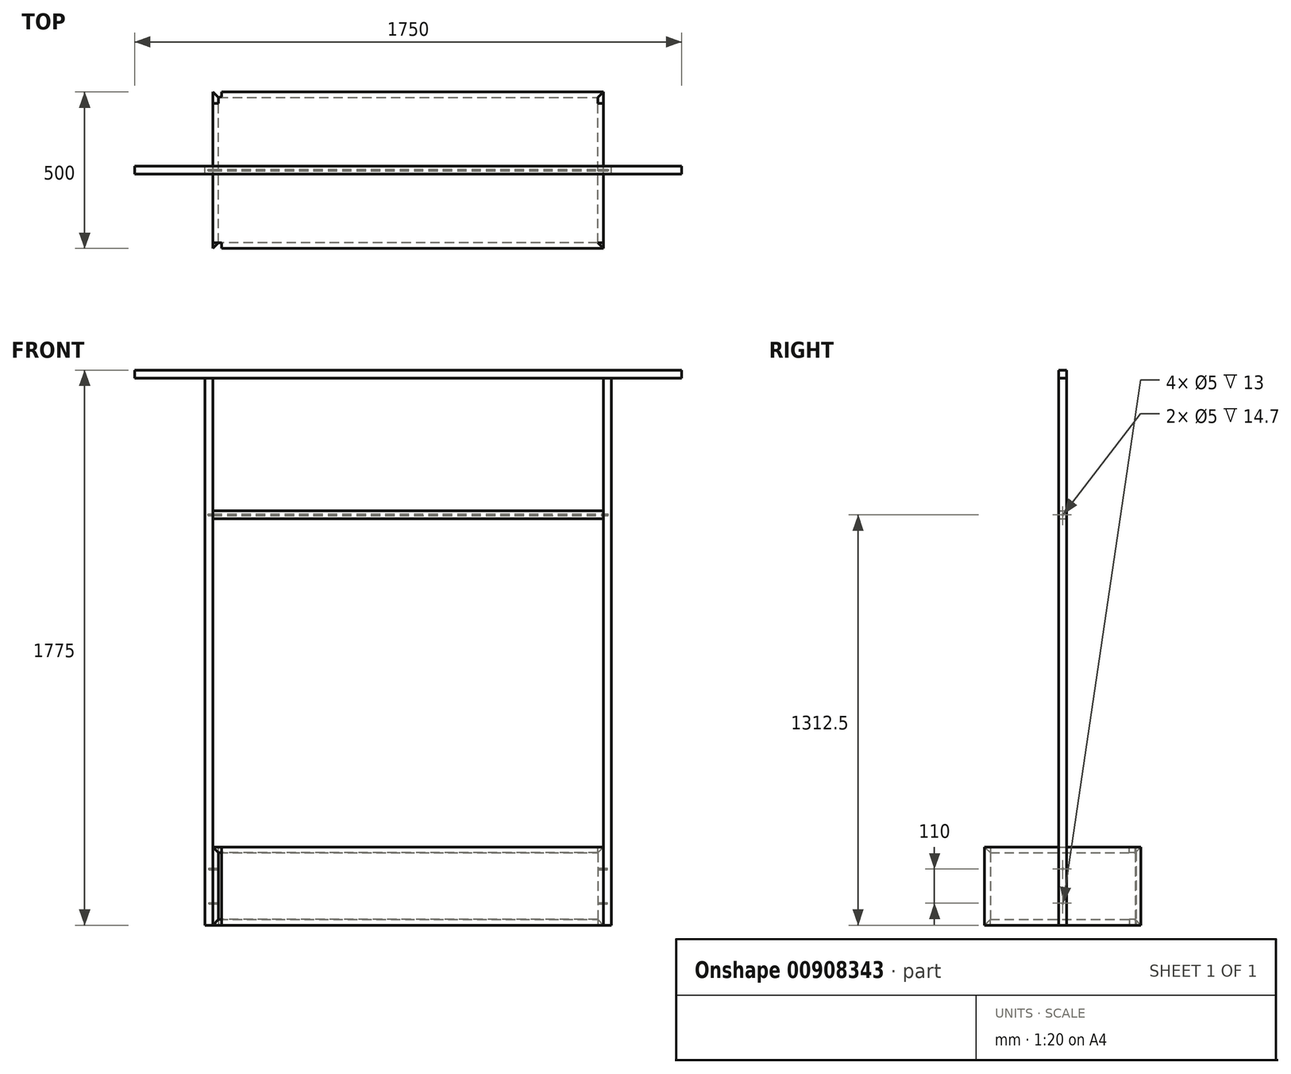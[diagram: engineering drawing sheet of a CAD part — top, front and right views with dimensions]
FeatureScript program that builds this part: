
annotation { "Feature Type Name" : "Feature", "Feature Type Description" : "" }
export const myFeature = defineFeature(function(context is Context, id is Id, definition is map)
    precondition{}
    {
        {
            var Q0;
            Q0=qCreatedBy(makeId("Front.planeOp"),FACE);
            var sketch = newSketch(context, id + "F0", { "sketchPlane" : qUnion([Q0])});
            skLineSegment(sketch, "E0", {"start": v(-625, 0) * mm, "end": v(625, 0) * mm});
            skLineSegment(sketch, "E1", {"start": v(625, 0) * mm, "end": v(607, 18) * mm});
            skLineSegment(sketch, "E2", {"start": v(607, 18) * mm, "end": v(-607, 18) * mm});
            skLineSegment(sketch, "E3", {"start": v(-607, 18) * mm, "end": v(-625, 0) * mm});
            skSolve(sketch);
        }
        {
            var Q0;
            Q0 = qSketchRegion(id + "F0", true);
            extrude(context, id + "F1", {"entities" : qUnion([Q0]), "endBound" : BoundingType.SYMMETRIC, "depth" : 500 * mm, "offsetDistance" : 25 * mm});
        }
        {
            var Q0;
            Q0=qCreatedBy(makeId("Right.planeOp"),FACE);
            var sketch = newSketch(context, id + "F2", { "sketchPlane" : qUnion([Q0])});
            skLineSegment(sketch, "E4", {"start": v(-250, 0) * mm, "end": v(-231.1, 18.9) * mm});
            skLineSegment(sketch, "E5", {"start": v(-231.1, 18.9) * mm, "end": v(-231.1, 28.41) * mm});
            skLineSegment(sketch, "E6", {"start": v(-231.1, 28.41) * mm, "end": v(-266.04, 28.41) * mm});
            skLineSegment(sketch, "E7", {"start": v(-266.04, 28.41) * mm, "end": v(-266.04, 0) * mm});
            skLineSegment(sketch, "E8", {"start": v(-266.04, 0) * mm, "end": v(-250, 0) * mm});
            skLineSegment(sketch, "E9", {"start": v(250, 0) * mm, "end": v(231.1, 18.9) * mm});
            skLineSegment(sketch, "E10", {"start": v(231.1, 18.9) * mm, "end": v(231.1, 44) * mm});
            skLineSegment(sketch, "E11", {"start": v(231.1, 44) * mm, "end": v(262.92, 44) * mm});
            skLineSegment(sketch, "E12", {"start": v(262.92, 44) * mm, "end": v(262.92, 0) * mm});
            skLineSegment(sketch, "E13", {"start": v(250, 0) * mm, "end": v(262.92, 0) * mm});
            skSolve(sketch);
        }
        {
            var Q0;
            Q0 = qSketchRegion(id + "F2", true);
            extrude(context, id + "F3", {"entities" : qUnion([Q0]), "operationType" : NewBodyOperationType.REMOVE, "endBound" : BoundingType.SYMMETRIC, "oppositeDirection" : true, "depth" : 1428 * mm, "offsetDistance" : 25 * mm});
        }
        {
            var Q0;
            Q0=qCreatedBy(makeId("Right.planeOp"),FACE);
            var sketch = newSketch(context, id + "F4", { "sketchPlane" : qUnion([Q0])});
            skLineSegment(sketch, "E14.0", {"start": v(232, 18) * mm, "end": v(250, 0) * mm});
            skLineSegment(sketch, "E14.1", {"start": v(-232, 18) * mm, "end": v(-250, 0) * mm});
            skLineSegment(sketch, "E15", {"start": v(232, 18) * mm, "end": v(232, 232) * mm});
            skLineSegment(sketch, "E16", {"start": v(232, 232) * mm, "end": v(250, 250) * mm});
            skLineSegment(sketch, "E17", {"start": v(250, 250) * mm, "end": v(250, 0) * mm});
            skLineSegment(sketch, "E18", {"start": v(-232, 18) * mm, "end": v(-232, 232) * mm});
            skLineSegment(sketch, "E19", {"start": v(-232, 232) * mm, "end": v(-250, 250) * mm});
            skLineSegment(sketch, "E20", {"start": v(-250, 250) * mm, "end": v(-250, 0) * mm});
            skSolve(sketch);
        }
        {
            var Q0;
            Q0=makeQuery(id+"F4.imprint","IMPRINT",FACE,{"disambiguationData":[TD([[makeQuery(id+"F4.imprint","IMPRINT",EDGE,{"derivedFrom":sQuery(id+"F4.wireOp",EDGE,"E14.0")}),1.0]])]});
            var Q1;
            Q1=makeQuery(id+"F4.imprint","IMPRINT",FACE,{"disambiguationData":[TD([[makeQuery(id+"F4.imprint","IMPRINT",EDGE,{"derivedFrom":sQuery(id+"F4.wireOp",EDGE,"E14.1")}),-1.0]])]});
            var Q2;
            Q2=makeQuery(id+"F1.opExtrude","CAP_VERTEX",VERTEX,{"disambiguationData":[OSD([sQuery(id+"F0.wireOp",EDGE,"E0"),sQuery(id+"F0.wireOp",EDGE,"E1")])],"isStart":true});
            extrude(context, id + "F5", {"entities" : qUnion([Q0, Q1]), "endBound" : BoundingType.SYMMETRIC, "depth" : 1250 * mm, "endBoundEntityVertex" : qUnion([Q2]), "offsetDistance" : 25 * mm});
        }
        {
            var Q0;
            Q0=qCreatedBy(makeId("Top.planeOp"),FACE);
            var sketch = newSketch(context, id + "F6", { "sketchPlane" : qUnion([Q0])});
            skLineSegment(sketch, "E21", {"start": v(-625, 250) * mm, "end": v(-607, 232) * mm});
            skLineSegment(sketch, "E22", {"start": v(-607, 232) * mm, "end": v(-607, 212.8) * mm});
            skLineSegment(sketch, "E23", {"start": v(-607, 212.8) * mm, "end": v(-625, 212.8) * mm});
            skLineSegment(sketch, "E24", {"start": v(-625, 212.8) * mm, "end": v(-625, 250) * mm});
            skLineSegment(sketch, "E25", {"start": v(-607, -232) * mm, "end": v(-625, -250) * mm});
            skLineSegment(sketch, "E26", {"start": v(-625, -250) * mm, "end": v(-638.85, -250) * mm});
            skLineSegment(sketch, "E27", {"start": v(-638.85, -250) * mm, "end": v(-638.85, -232) * mm});
            skLineSegment(sketch, "E28", {"start": v(-638.85, -232) * mm, "end": v(-607, -232) * mm});
            skLineSegment(sketch, "E29.MirrorCS", {"start": v(625, 250) * mm, "end": v(607, 232) * mm});
            skLineSegment(sketch, "E30.MirrorCS", {"start": v(638.85, -232) * mm, "end": v(607, -232) * mm});
            skLineSegment(sketch, "E31.MirrorCS", {"start": v(638.85, -250) * mm, "end": v(638.85, -232) * mm});
            skLineSegment(sketch, "E32.MirrorCS", {"start": v(607, -232) * mm, "end": v(625, -250) * mm});
            skLineSegment(sketch, "E33.MirrorCS", {"start": v(607, 232) * mm, "end": v(607, 212.8) * mm});
            skLineSegment(sketch, "E34.MirrorCS", {"start": v(625, -250) * mm, "end": v(638.85, -250) * mm});
            skLineSegment(sketch, "E35.MirrorCS", {"start": v(607, 212.8) * mm, "end": v(625, 212.8) * mm});
            skLineSegment(sketch, "E36.MirrorCS", {"start": v(625, 212.8) * mm, "end": v(625, 250) * mm});
            skSolve(sketch);
        }
        {
            var Q0;
            Q0 = qSketchRegion(id + "F6", true);
            extrude(context, id + "F7", {"entities" : qUnion([Q0]), "operationType" : NewBodyOperationType.REMOVE, "endBound" : BoundingType.SYMMETRIC, "depth" : 1216 * mm, "offsetDistance" : 25 * mm});
        }
        {
            var Q0;
            Q0=qCreatedBy(makeId("Front.planeOp"),FACE);
            var sketch = newSketch(context, id + "F8", { "sketchPlane" : qUnion([Q0])});
            skLineSegment(sketch, "E37.0", {"start": v(-625, 0) * mm, "end": v(-607, 18) * mm});
            skLineSegment(sketch, "E37.1", {"start": v(-607, 232) * mm, "end": v(-607, 18) * mm});
            skLineSegment(sketch, "E37.2", {"start": v(-625, 250) * mm, "end": v(-625, 0) * mm});
            skLineSegment(sketch, "E37.3", {"start": v(-607, 232) * mm, "end": v(-625, 250) * mm});
            skSolve(sketch);
        }
        {
            var Q0;
            Q0 = qSketchRegion(id + "F8", true);
            extrude(context, id + "F9", {"entities" : qUnion([Q0]), "endBound" : BoundingType.SYMMETRIC, "depth" : 500 * mm, "offsetDistance" : 25 * mm});
        }
        {
            var Q0;
            Q0=qCreatedBy(makeId("Top.planeOp"),FACE);
            var sketch = newSketch(context, id + "F10", { "sketchPlane" : qUnion([Q0])});
            skLineSegment(sketch, "E38.0", {"start": v(-607, -232) * mm, "end": v(-625, -250) * mm});
            skLineSegment(sketch, "E38.1", {"start": v(-607, 232) * mm, "end": v(-625, 250) * mm});
            skLineSegment(sketch, "E39", {"start": v(-625, 250) * mm, "end": v(-625, 288.49) * mm});
            skLineSegment(sketch, "E40", {"start": v(-625, 288.49) * mm, "end": v(-596.8, 288.49) * mm});
            skLineSegment(sketch, "E41", {"start": v(-596.8, 288.49) * mm, "end": v(-596.8, 234.6) * mm});
            skLineSegment(sketch, "E42", {"start": v(-596.8, 234.6) * mm, "end": v(-607, 232) * mm});
            skLineSegment(sketch, "E43", {"start": v(-607, -232) * mm, "end": v(-596.8, -232) * mm});
            skLineSegment(sketch, "E44", {"start": v(-596.8, -232) * mm, "end": v(-596.8, -280.72) * mm});
            skLineSegment(sketch, "E45", {"start": v(-596.8, -280.72) * mm, "end": v(-625, -280.72) * mm});
            skLineSegment(sketch, "E46", {"start": v(-625, -280.72) * mm, "end": v(-625, -250) * mm});
            skSolve(sketch);
        }
        {
            var Q0;
            Q0 = qSketchRegion(id + "F10", true);
            extrude(context, id + "F11", {"entities" : qUnion([Q0]), "operationType" : NewBodyOperationType.REMOVE, "endBound" : BoundingType.SYMMETRIC, "depth" : 1068 * mm, "offsetDistance" : 25 * mm});
        }
        {
            var Q0;
            Q0=makeQuery(id+"F9.opExtrude","SWEPT_BODY",BODY,{"disambiguationData":[OSD([sQuery(id+"F8.wireOp",EDGE,"E37.0"),sQuery(id+"F8.wireOp",EDGE,"E37.1"),sQuery(id+"F8.wireOp",EDGE,"E37.2"),sQuery(id+"F8.wireOp",EDGE,"E37.3")])]});
            var Q1;
            Q1=qCreatedBy(makeId("Right.planeOp"),FACE);
            mirror(context, id + "F12", {"entities" : qUnion([Q0]), "mirrorPlane" : qUnion([Q1])});
        }
        {
            var Q0;
            Q0=qCreatedBy(makeId("Top.planeOp"),FACE);
            cPlane(context, id + "F13", {"entities" : qUnion([Q0]), "cplaneType" : CPlaneType.OFFSET, "offset" : 125 * mm, "width" : 150 * mm, "height" : 150 * mm});
        }
        {
            var Q0;
            Q0=makeQuery(id+"F1.opExtrude","SWEPT_BODY",BODY,{"disambiguationData":[OSD([sQuery(id+"F0.wireOp",EDGE,"E0"),sQuery(id+"F0.wireOp",EDGE,"E1"),sQuery(id+"F0.wireOp",EDGE,"E2"),sQuery(id+"F0.wireOp",EDGE,"E3")])]});
            var Q1;
            Q1=qCreatedBy(id+"F13.planeOp",FACE);
            mirror(context, id + "F14", {"entities" : qUnion([Q0]), "mirrorPlane" : qUnion([Q1])});
        }
        {
            var Q0;
            Q0=qCreatedBy(makeId("Front.planeOp"),FACE);
            var sketch = newSketch(context, id + "F15", { "sketchPlane" : qUnion([Q0])});
            skLineSegment(sketch, "E47.bottom", {"start": v(625, 0) * mm, "end": v(650, 0) * mm});
            skLineSegment(sketch, "E47.top", {"start": v(625, 1750) * mm, "end": v(650, 1750) * mm});
            skLineSegment(sketch, "E47.left", {"start": v(625, 0) * mm, "end": v(625, 1750) * mm});
            skLineSegment(sketch, "E47.right", {"start": v(650, 0) * mm, "end": v(650, 1750) * mm});
            skLineSegment(sketch, "E48.bottom", {"start": v(-625, 0) * mm, "end": v(-650, 0) * mm});
            skLineSegment(sketch, "E48.top", {"start": v(-625, 1750) * mm, "end": v(-650, 1750) * mm});
            skLineSegment(sketch, "E48.left", {"start": v(-625, 0) * mm, "end": v(-625, 1750) * mm});
            skLineSegment(sketch, "E48.right", {"start": v(-650, 0) * mm, "end": v(-650, 1750) * mm});
            skSolve(sketch);
        }
        {
            var Q0;
            Q0 = qSketchRegion(id + "F15", true);
            extrude(context, id + "F16", {"entities" : qUnion([Q0]), "endBound" : BoundingType.SYMMETRIC, "depth" : 25 * mm, "offsetDistance" : 25 * mm});
        }
        {
            var Q0;
            Q0=qCreatedBy(makeId("Front.planeOp"),FACE);
            var sketch = newSketch(context, id + "F17", { "sketchPlane" : qUnion([Q0])});
            skLineSegment(sketch, "E49.bottom", {"start": v(-875, 1750) * mm, "end": v(875, 1750) * mm});
            skLineSegment(sketch, "E49.top", {"start": v(-875, 1775) * mm, "end": v(875, 1775) * mm});
            skLineSegment(sketch, "E49.left", {"start": v(-875, 1750) * mm, "end": v(-875, 1775) * mm});
            skLineSegment(sketch, "E49.right", {"start": v(875, 1750) * mm, "end": v(875, 1775) * mm});
            skPoint(sketch, "E50", {"position": v(0, 1750) * mm});
            skSolve(sketch);
        }
        {
            var Q0;
            Q0 = qSketchRegion(id + "F17", true);
            extrude(context, id + "F18", {"entities" : qUnion([Q0]), "endBound" : BoundingType.SYMMETRIC, "depth" : 25 * mm, "offsetDistance" : 25 * mm});
        }
        {
            var Q0;
            Q0=makeQuery(id+"F16.opExtrude","SWEPT_FACE",FACE,{"disambiguationData":[OSD([sQuery(id+"F15.wireOp",EDGE,"E48.left")])]});
            var sketch = newSketch(context, id + "F19", { "sketchPlane" : qUnion([Q0])});
            skLineSegment(sketch, "E51.bottom", {"start": v(12.5, 1300) * mm, "end": v(-12.5, 1300) * mm});
            skLineSegment(sketch, "E51.top", {"start": v(12.5, 1325) * mm, "end": v(-12.5, 1325) * mm});
            skLineSegment(sketch, "E51.left", {"start": v(12.5, 1300) * mm, "end": v(12.5, 1325) * mm});
            skLineSegment(sketch, "E51.right", {"start": v(-12.5, 1300) * mm, "end": v(-12.5, 1325) * mm});
            skSolve(sketch);
        }
        {
            var Q0;
            Q0 = qSketchRegion(id + "F19", true);
            var Q1;
            Q1=makeQuery(id+"F16.opExtrude","SWEPT_FACE",FACE,{"disambiguationData":[OSD([sQuery(id+"F15.wireOp",EDGE,"E47.left")])]});
            extrude(context, id + "F20", {"entities" : qUnion([Q0]), "endBound" : BoundingType.UP_TO_SURFACE, "depth" : 25 * mm, "endBoundEntityFace" : qUnion([Q1]), "offsetDistance" : 25 * mm});
        }
        {
            var Q0;
            Q0=qCreatedBy(makeId("Right.planeOp"),FACE);
            var sketch = newSketch(context, id + "F21", { "sketchPlane" : qUnion([Q0])});
            skCircle(sketch, "E52", {"center": v(0, 180) * mm, "radius": 2.5 * mm});
            skCircle(sketch, "E53", {"center": v(0, 70) * mm, "radius": 2.5 * mm});
            skSolve(sketch);
        }
        {
            var Q0;
            Q0 = qSketchRegion(id + "F21", true);
            extrude(context, id + "F22", {"entities" : qUnion([Q0]), "operationType" : NewBodyOperationType.REMOVE, "endBound" : BoundingType.SYMMETRIC, "oppositeDirection" : true, "depth" : 1276 * mm, "offsetDistance" : 25 * mm});
        }
        {
            var Q0;
            Q0=qCreatedBy(makeId("Right.planeOp"),FACE);
            var sketch = newSketch(context, id + "F23", { "sketchPlane" : qUnion([Q0])});
            skCircle(sketch, "E54", {"center": v(0, 1312.5) * mm, "radius": 2.5 * mm});
            skSolve(sketch);
        }
        {
            var Q0;
            Q0 = qSketchRegion(id + "F23", true);
            extrude(context, id + "F24", {"entities" : qUnion([Q0]), "operationType" : NewBodyOperationType.REMOVE, "endBound" : BoundingType.SYMMETRIC, "oppositeDirection" : true, "depth" : 1279.4 * mm, "offsetDistance" : 25 * mm});
        }
    });
